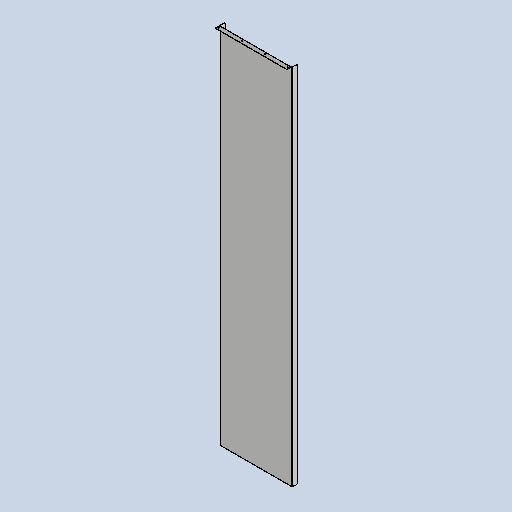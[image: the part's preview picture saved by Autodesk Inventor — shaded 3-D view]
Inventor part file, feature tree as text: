
AUTODESK INVENTOR PART (.ipt)
format: ipt  version: 2025 (Build 290162010, 162A)  size: 246,272 bytes
history: native  units: mm
features: sheet_metal_op x7, sketch x7, other x5, extrude x4, reference x4, projected_geometry x2, mirror x1
ambient origin geometry x8: Origin, YZ Plane, XZ Plane, XY Plane, X Axis, Y Axis, Z Axis, Center Point
bodies: Solid1 (feature_tree)
feature tree (30):
  sheet_metal_op  "Face1"
  sheet_metal_op  "Flange1"
  sheet_metal_op  "Flange2"
  extrude  "Extrusion1"  Depth=400.0mm
  extrude  "Extrusion2"  Depth=2.0mm
  extrude  "Extrusion3"  Depth=4.0mm
  extrude  "Extrusion4"  Depth=30.0mm TaperAngle=90.0deg
  mirror  "Mirror1"
  sketch  "Sketch1"  dims[d0=2011.081mm d1=400.0mm]
  other  "Plate1"
  sketch  "Sketch2"  dims[d2=2.0mm d3=2.0mm]
  other  "Plate2"
  sheet_metal_op  "Bend1"
  sheet_metal_op  "Corner1"
  sketch  "Sketch3"  dims[d4=1.0mm d5=4.0mm]
  projected_geometry  "Projected Loop1"
  sketch  "Sketch4"  dims[d6=2.75mm d7=30.0mm d8=90.0deg d9=2.75mm]
  other  "Plate3"
  sheet_metal_op  "Bend2"
  sheet_metal_op  "Corner2"
  sketch  "Sketch5"  dims[d10=8.0mm]
  sketch  "Sketch6"  dims[d11=2.0mm]
  reference  "Reference1"
  reference  "Reference2"
  reference  "Reference3"
  reference  "Reference4"
  sketch  "Sketch7"  dims[d12=2.75mm d13=1.001819mm d14=0.0mm d15=0.0mm d16=2.0mm d17=1.0mm d18=4.0mm d19=2.75mm d20=30.0mm d21=14.706144mm d22=2.75mm d23=8.0mm d24=2.0mm d25=2.75mm d26=1.001819mm d27=0.0mm d28=0.0mm d29=10.0mm d30=0.0mm d31=2.0mm d32=0.0mm]
  projected_geometry  "Projected Loop2"
  other  "ASY MSC 001 отстойник осветлитель.iam"
  other  "MSC 073 ridge 3.ipt:1"
